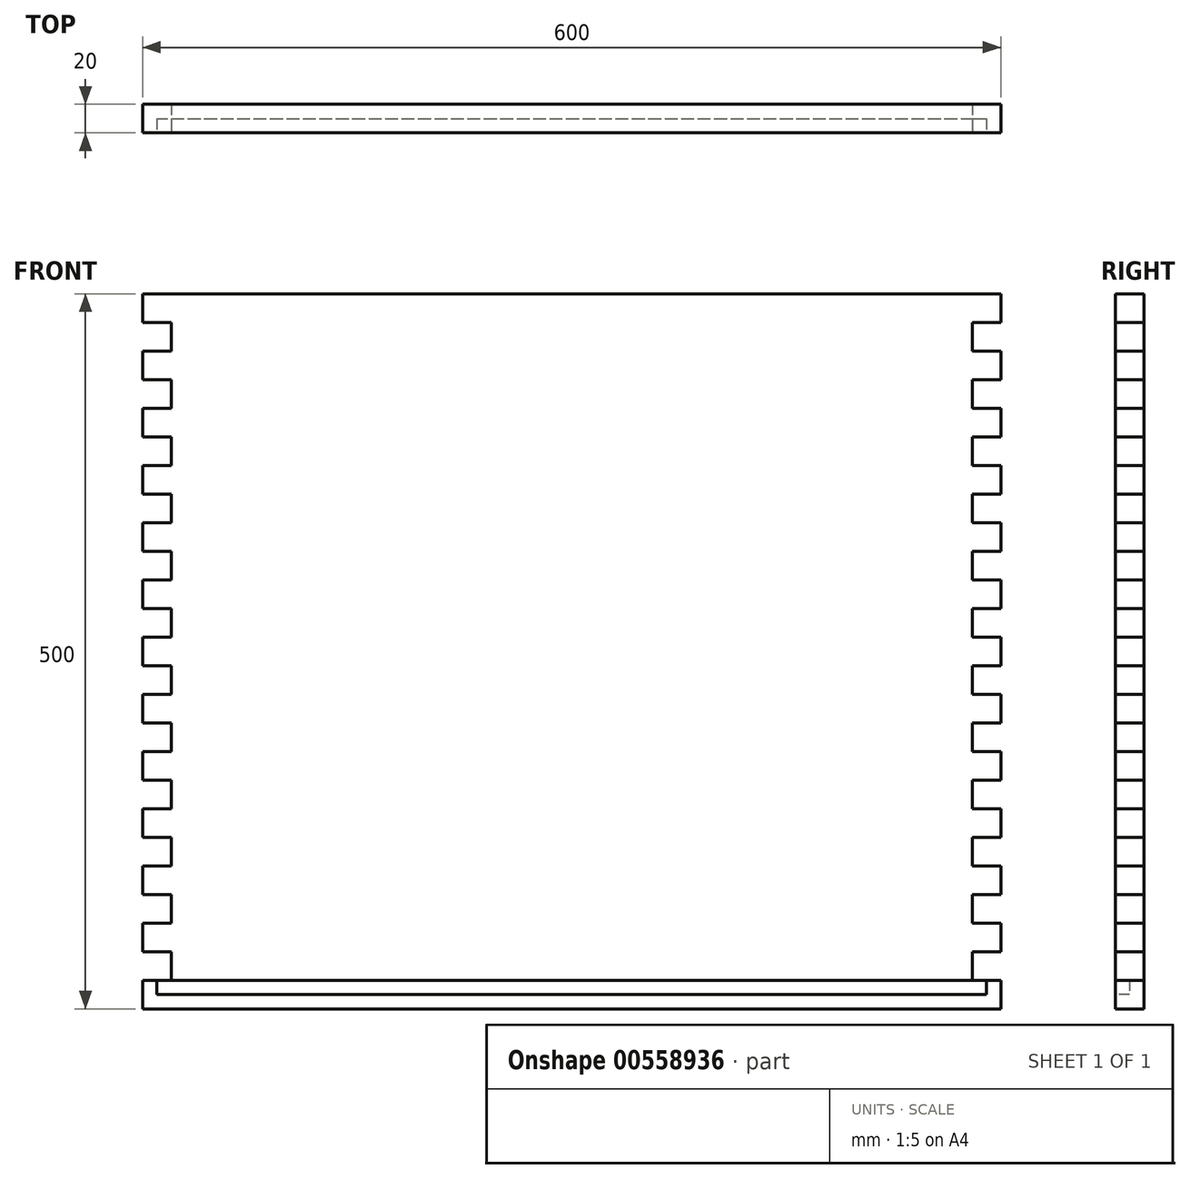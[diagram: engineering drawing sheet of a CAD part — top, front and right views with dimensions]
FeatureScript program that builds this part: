
annotation { "Feature Type Name" : "Feature", "Feature Type Description" : "" }
export const myFeature = defineFeature(function(context is Context, id is Id, definition is map)
    precondition{}
    {
        {
            var Q0;
            Q0=qCreatedBy(makeId("Front.planeOp"),FACE);
            var sketch = newSketch(context, id + "F0", { "sketchPlane" : qUnion([Q0])});
            skLineSegment(sketch, "E0.bottom", {"start": v(300, -250) * mm, "end": v(-300, -250) * mm});
            skLineSegment(sketch, "E0.top", {"start": v(300, 250) * mm, "end": v(-300, 250) * mm});
            skLineSegment(sketch, "E0.left", {"start": v(300, -250) * mm, "end": v(300, 250) * mm});
            skLineSegment(sketch, "E0.right", {"start": v(-300, -250) * mm, "end": v(-300, 250) * mm});
            skPoint(sketch, "E0.middle", {"position": v(0, 0) * mm});
            skSolve(sketch);
        }
        {
            var Q0;
            Q0 = qSketchRegion(id + "F0", true);
            extrude(context, id + "F1", {"entities" : qUnion([Q0]), "depth" : 20 * mm, "offsetDistance" : 25 * mm});
        }
        {
            var Q0;
            Q0=makeQuery(id+"F1.opExtrude","CAP_FACE",FACE,{"disambiguationData":[OSD([sQuery(id+"F0.wireOp",EDGE,"E0.bottom"),sQuery(id+"F0.wireOp",EDGE,"E0.top"),sQuery(id+"F0.wireOp",EDGE,"E0.left"),sQuery(id+"F0.wireOp",EDGE,"E0.right")])],"isStart":false});
            var sketch = newSketch(context, id + "F2", { "sketchPlane" : qUnion([Q0])});
            skLineSegment(sketch, "E1.bottom", {"start": v(300, -230) * mm, "end": v(280, -230) * mm});
            skLineSegment(sketch, "E1.top", {"start": v(300, -210) * mm, "end": v(280, -210) * mm});
            skLineSegment(sketch, "E1.left", {"start": v(300, -230) * mm, "end": v(300, -210) * mm});
            skLineSegment(sketch, "E1.right", {"start": v(280, -230) * mm, "end": v(280, -210) * mm});
            skLineSegment(sketch, "E2.0.1.0", {"start": v(300, -170) * mm, "end": v(280, -170) * mm});
            skLineSegment(sketch, "E2.0.1.1", {"start": v(280, -190) * mm, "end": v(280, -170) * mm});
            skLineSegment(sketch, "E2.0.1.2", {"start": v(300, -190) * mm, "end": v(280, -190) * mm});
            skLineSegment(sketch, "E2.0.1.3", {"start": v(300, -190) * mm, "end": v(300, -170) * mm});
            skLineSegment(sketch, "E2.0.2.0", {"start": v(300, -130) * mm, "end": v(280, -130) * mm});
            skLineSegment(sketch, "E2.0.2.1", {"start": v(280, -150) * mm, "end": v(280, -130) * mm});
            skLineSegment(sketch, "E2.0.2.2", {"start": v(300, -150) * mm, "end": v(280, -150) * mm});
            skLineSegment(sketch, "E2.0.2.3", {"start": v(300, -150) * mm, "end": v(300, -130) * mm});
            skLineSegment(sketch, "E2.0.3.0", {"start": v(300, -90) * mm, "end": v(280, -90) * mm});
            skLineSegment(sketch, "E2.0.3.1", {"start": v(280, -110) * mm, "end": v(280, -90) * mm});
            skLineSegment(sketch, "E2.0.3.2", {"start": v(300, -110) * mm, "end": v(280, -110) * mm});
            skLineSegment(sketch, "E2.0.3.3", {"start": v(300, -110) * mm, "end": v(300, -90) * mm});
            skLineSegment(sketch, "E2.0.4.0", {"start": v(300, -50) * mm, "end": v(280, -50) * mm});
            skLineSegment(sketch, "E2.0.4.1", {"start": v(280, -70) * mm, "end": v(280, -50) * mm});
            skLineSegment(sketch, "E2.0.4.2", {"start": v(300, -70) * mm, "end": v(280, -70) * mm});
            skLineSegment(sketch, "E2.0.4.3", {"start": v(300, -70) * mm, "end": v(300, -50) * mm});
            skLineSegment(sketch, "E2.0.5.0", {"start": v(300, -10) * mm, "end": v(280, -10) * mm});
            skLineSegment(sketch, "E2.0.5.1", {"start": v(280, -30) * mm, "end": v(280, -10) * mm});
            skLineSegment(sketch, "E2.0.5.2", {"start": v(300, -30) * mm, "end": v(280, -30) * mm});
            skLineSegment(sketch, "E2.0.5.3", {"start": v(300, -30) * mm, "end": v(300, -10) * mm});
            skLineSegment(sketch, "E2.0.6.0", {"start": v(300, 30) * mm, "end": v(280, 30) * mm});
            skLineSegment(sketch, "E2.0.6.1", {"start": v(280, 10) * mm, "end": v(280, 30) * mm});
            skLineSegment(sketch, "E2.0.6.2", {"start": v(300, 10) * mm, "end": v(280, 10) * mm});
            skLineSegment(sketch, "E2.0.6.3", {"start": v(300, 10) * mm, "end": v(300, 30) * mm});
            skLineSegment(sketch, "E2.0.7.0", {"start": v(300, 70) * mm, "end": v(280, 70) * mm});
            skLineSegment(sketch, "E2.0.7.1", {"start": v(280, 50) * mm, "end": v(280, 70) * mm});
            skLineSegment(sketch, "E2.0.7.2", {"start": v(300, 50) * mm, "end": v(280, 50) * mm});
            skLineSegment(sketch, "E2.0.7.3", {"start": v(300, 50) * mm, "end": v(300, 70) * mm});
            skLineSegment(sketch, "E2.0.8.0", {"start": v(300, 110) * mm, "end": v(280, 110) * mm});
            skLineSegment(sketch, "E2.0.8.1", {"start": v(280, 90) * mm, "end": v(280, 110) * mm});
            skLineSegment(sketch, "E2.0.8.2", {"start": v(300, 90) * mm, "end": v(280, 90) * mm});
            skLineSegment(sketch, "E2.0.8.3", {"start": v(300, 90) * mm, "end": v(300, 110) * mm});
            skLineSegment(sketch, "E2.0.9.0", {"start": v(300, 150) * mm, "end": v(280, 150) * mm});
            skLineSegment(sketch, "E2.0.9.1", {"start": v(280, 130) * mm, "end": v(280, 150) * mm});
            skLineSegment(sketch, "E2.0.9.2", {"start": v(300, 130) * mm, "end": v(280, 130) * mm});
            skLineSegment(sketch, "E2.0.9.3", {"start": v(300, 130) * mm, "end": v(300, 150) * mm});
            skLineSegment(sketch, "E2.0.10.0", {"start": v(300, 190) * mm, "end": v(280, 190) * mm});
            skLineSegment(sketch, "E2.0.10.1", {"start": v(280, 170) * mm, "end": v(280, 190) * mm});
            skLineSegment(sketch, "E2.0.10.2", {"start": v(300, 170) * mm, "end": v(280, 170) * mm});
            skLineSegment(sketch, "E2.0.10.3", {"start": v(300, 170) * mm, "end": v(300, 190) * mm});
            skLineSegment(sketch, "E2.direction1", {"start": v(280, -210) * mm, "end": v(305, -210) * mm, "construction": true});
            skLineSegment(sketch, "E2.direction2", {"start": v(280, -210) * mm, "end": v(280, -170) * mm, "construction": true});
            skLineSegment(sketch, "E3.MirrorCS", {"start": v(-300, -210) * mm, "end": v(-280, -210) * mm});
            skLineSegment(sketch, "E4.MirrorCS", {"start": v(-300, -70) * mm, "end": v(-300, -50) * mm});
            skLineSegment(sketch, "E5.MirrorCS", {"start": v(-300, 90) * mm, "end": v(-300, 110) * mm});
            skLineSegment(sketch, "E6.MirrorCS", {"start": v(-300, 10) * mm, "end": v(-280, 10) * mm});
            skLineSegment(sketch, "E7.MirrorCS", {"start": v(-300, 170) * mm, "end": v(-280, 170) * mm});
            skLineSegment(sketch, "E8.MirrorCS", {"start": v(-300, -70) * mm, "end": v(-280, -70) * mm});
            skLineSegment(sketch, "E9.MirrorCS", {"start": v(-300, 90) * mm, "end": v(-280, 90) * mm});
            skLineSegment(sketch, "E10.MirrorCS", {"start": v(-300, -30) * mm, "end": v(-280, -30) * mm});
            skLineSegment(sketch, "E11.MirrorCS", {"start": v(-300, 130) * mm, "end": v(-280, 130) * mm});
            skLineSegment(sketch, "E12.MirrorCS", {"start": v(-300, 50) * mm, "end": v(-300, 70) * mm});
            skLineSegment(sketch, "E13.MirrorCS", {"start": v(-300, -90) * mm, "end": v(-280, -90) * mm});
            skLineSegment(sketch, "E14.MirrorCS", {"start": v(-280, 10) * mm, "end": v(-280, 30) * mm});
            skLineSegment(sketch, "E15.MirrorCS", {"start": v(-280, 170) * mm, "end": v(-280, 190) * mm});
            skLineSegment(sketch, "E16.MirrorCS", {"start": v(-300, -150) * mm, "end": v(-300, -130) * mm});
            skLineSegment(sketch, "E17.MirrorCS", {"start": v(-300, -150) * mm, "end": v(-280, -150) * mm});
            skLineSegment(sketch, "E18.MirrorCS", {"start": v(-280, -150) * mm, "end": v(-280, -130) * mm});
            skLineSegment(sketch, "E19.MirrorCS", {"start": v(-300, -130) * mm, "end": v(-280, -130) * mm});
            skLineSegment(sketch, "E20.MirrorCS", {"start": v(-300, -190) * mm, "end": v(-300, -170) * mm});
            skLineSegment(sketch, "E21.MirrorCS", {"start": v(-300, -190) * mm, "end": v(-280, -190) * mm});
            skLineSegment(sketch, "E22.MirrorCS", {"start": v(-280, -190) * mm, "end": v(-280, -170) * mm});
            skLineSegment(sketch, "E23.MirrorCS", {"start": v(-300, -170) * mm, "end": v(-280, -170) * mm});
            skLineSegment(sketch, "E24.MirrorCS", {"start": v(-280, -230) * mm, "end": v(-280, -210) * mm});
            skLineSegment(sketch, "E25.MirrorCS", {"start": v(-300, -230) * mm, "end": v(-300, -210) * mm});
            skLineSegment(sketch, "E26.MirrorCS", {"start": v(-300, -230) * mm, "end": v(-280, -230) * mm});
            skLineSegment(sketch, "E27.MirrorCS", {"start": v(-300, -110) * mm, "end": v(-300, -90) * mm});
            skLineSegment(sketch, "E28.MirrorCS", {"start": v(-300, -110) * mm, "end": v(-280, -110) * mm});
            skLineSegment(sketch, "E29.MirrorCS", {"start": v(-280, -110) * mm, "end": v(-280, -90) * mm});
            skLineSegment(sketch, "E30.MirrorCS", {"start": v(-280, -70) * mm, "end": v(-280, -50) * mm});
            skLineSegment(sketch, "E31.MirrorCS", {"start": v(-280, 90) * mm, "end": v(-280, 110) * mm});
            skLineSegment(sketch, "E32.MirrorCS", {"start": v(-280, -30) * mm, "end": v(-280, -10) * mm});
            skLineSegment(sketch, "E33.MirrorCS", {"start": v(-280, 130) * mm, "end": v(-280, 150) * mm});
            skLineSegment(sketch, "E34.MirrorCS", {"start": v(-300, 50) * mm, "end": v(-280, 50) * mm});
            skLineSegment(sketch, "E35.MirrorCS", {"start": v(-300, 30) * mm, "end": v(-280, 30) * mm});
            skLineSegment(sketch, "E36.MirrorCS", {"start": v(-300, 190) * mm, "end": v(-280, 190) * mm});
            skLineSegment(sketch, "E37.MirrorCS", {"start": v(-300, 70) * mm, "end": v(-280, 70) * mm});
            skLineSegment(sketch, "E38.MirrorCS", {"start": v(-280, -210) * mm, "end": v(-280, -170) * mm, "construction": true});
            skLineSegment(sketch, "E39.MirrorCS", {"start": v(-280, -210) * mm, "end": v(-305, -210) * mm, "construction": true});
            skLineSegment(sketch, "E40.MirrorCS", {"start": v(-300, -50) * mm, "end": v(-280, -50) * mm});
            skLineSegment(sketch, "E41.MirrorCS", {"start": v(-300, 110) * mm, "end": v(-280, 110) * mm});
            skLineSegment(sketch, "E42.MirrorCS", {"start": v(-300, -10) * mm, "end": v(-280, -10) * mm});
            skLineSegment(sketch, "E43.MirrorCS", {"start": v(-300, 10) * mm, "end": v(-300, 30) * mm});
            skLineSegment(sketch, "E44.MirrorCS", {"start": v(-300, 170) * mm, "end": v(-300, 190) * mm});
            skLineSegment(sketch, "E45.MirrorCS", {"start": v(-300, 150) * mm, "end": v(-280, 150) * mm});
            skLineSegment(sketch, "E46.MirrorCS", {"start": v(-280, 50) * mm, "end": v(-280, 70) * mm});
            skLineSegment(sketch, "E47.MirrorCS", {"start": v(-300, -30) * mm, "end": v(-300, -10) * mm});
            skLineSegment(sketch, "E48.MirrorCS", {"start": v(-300, 130) * mm, "end": v(-300, 150) * mm});
            skLineSegment(sketch, "E49.0.0.11", {"start": v(300, 230) * mm, "end": v(280, 230) * mm});
            skLineSegment(sketch, "E49.3.0.11", {"start": v(280, 210) * mm, "end": v(280, 230) * mm});
            skLineSegment(sketch, "E49.6.0.11", {"start": v(300, 210) * mm, "end": v(280, 210) * mm});
            skLineSegment(sketch, "E49.9.0.11", {"start": v(300, 210) * mm, "end": v(300, 230) * mm});
            skLineSegment(sketch, "E50.MirrorCS", {"start": v(-280, 210) * mm, "end": v(-280, 230) * mm});
            skLineSegment(sketch, "E51.MirrorCS", {"start": v(-300, 230) * mm, "end": v(-280, 230) * mm});
            skLineSegment(sketch, "E52.MirrorCS", {"start": v(-300, 210) * mm, "end": v(-300, 230) * mm});
            skLineSegment(sketch, "E53.MirrorCS", {"start": v(-300, 210) * mm, "end": v(-280, 210) * mm});
            skSolve(sketch);
        }
        {
            var Q0;
            Q0 = qSketchRegion(id + "F2", true);
            extrude(context, id + "F3", {"entities" : qUnion([Q0]), "operationType" : NewBodyOperationType.REMOVE, "endBound" : BoundingType.UP_TO_NEXT, "oppositeDirection" : true, "depth" : 25 * mm, "offsetDistance" : 25 * mm});
        }
        {
            var Q0;
            Q0=makeQuery(id+"F1.opExtrude","CAP_FACE",FACE,{"disambiguationData":[OSD([sQuery(id+"F0.wireOp",EDGE,"E0.bottom"),sQuery(id+"F0.wireOp",EDGE,"E0.top"),sQuery(id+"F0.wireOp",EDGE,"E0.left"),sQuery(id+"F0.wireOp",EDGE,"E0.right")])],"isStart":false});
            var sketch = newSketch(context, id + "F4", { "sketchPlane" : qUnion([Q0])});
            skLineSegment(sketch, "E54.bottom", {"start": v(-290, -230) * mm, "end": v(290, -230) * mm});
            skLineSegment(sketch, "E54.top", {"start": v(-290, -240) * mm, "end": v(290, -240) * mm});
            skLineSegment(sketch, "E54.left", {"start": v(-290, -230) * mm, "end": v(-290, -240) * mm});
            skLineSegment(sketch, "E54.right", {"start": v(290, -230) * mm, "end": v(290, -240) * mm});
            skPoint(sketch, "E54.middle", {"position": v(0, -235) * mm});
            skSolve(sketch);
        }
        {
            var Q0;
            Q0 = qSketchRegion(id + "F4", true);
            extrude(context, id + "F5", {"entities" : qUnion([Q0]), "operationType" : NewBodyOperationType.REMOVE, "oppositeDirection" : true, "depth" : 10 * mm, "offsetDistance" : 25 * mm});
        }
    });
